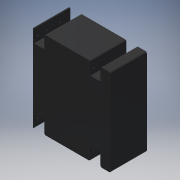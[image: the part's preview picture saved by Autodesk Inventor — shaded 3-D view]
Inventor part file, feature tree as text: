
AUTODESK INVENTOR PART (.ipt)
format: ipt  version: 2016 (Build 200138000, 138)  size: 579,072 bytes
history: native  units: mm
features: extrude x26, sketch x26, fillet x1
ambient origin geometry x8: Origin, YZ Plane, XZ Plane, XY Plane, X Axis, Y Axis, Z Axis, Center Point
bodies: Solid1 (feature_tree)
feature tree (53):
  extrude  "Extrusion1"  Depth=20.0mm
  extrude  "Extrusion2"  Depth=170.0mm
  extrude  "Extrusion3"  Depth=25.0mm
  extrude  "Extrusion4"  Depth=25.0mm
  extrude  "Extrusion5"  Depth=20.0mm
  extrude  "Extrusion6"  Depth=20.0mm
  extrude  "Extrusion7"  Depth=90.0mm
  extrude  "Extrusion8"  Depth=2.0mm TaperAngle=0.0deg
  extrude  "Extrusion9"  Depth=2.0mm
  extrude  "Extrusion10"  Depth=2.0mm
  extrude  "Extrusion11"  Depth=2.0mm
  extrude  "Extrusion12"  Depth=2.0mm
  extrude  "Extrusion13"  Depth=2.0mm
  extrude  "Extrusion14"  Depth=2.0mm
  extrude  "Extrusion15"  Depth=2.0mm
  extrude  "Extrusion16"  Depth=69.0mm TaperAngle=0.0deg
  extrude  "Extrusion17"  Depth=10.0mm TaperAngle=0.0deg
  extrude  "Extrusion18"  Depth=10.0mm
  extrude  "Extrusion32"  Depth=4.0mm TaperAngle=0.0deg
  extrude  "Extrusion33"  Depth=10.0mm
  extrude  "Extrusion34"  Depth=4.0mm TaperAngle=0.0deg
  extrude  "Extrusion35"  Depth=10.0mm
  extrude  "Extrusion53"  Depth=4.0mm TaperAngle=0.0deg
  fillet  "Fillet1"  Radius=7.0mm
  extrude  "Extrusion54"  Depth=10.0mm
  extrude  "Extrusion55"  Depth=4.0mm
  extrude  "Extrusion56"  Depth=2.0mm
  sketch  "Sketch1"  dims[d0=2.0mm d1=20.0mm]
  sketch  "Sketch2"  dims[d2=20.0mm d3=170.0mm]
  sketch  "Sketch4"  dims[d4=170.0mm d6=25.0mm]
  sketch  "Sketch5"  dims[d9=25.0mm d10=25.0mm]
  sketch  "Sketch6"  dims[d11=25.0mm d12=20.0mm]
  sketch  "Sketch7"  dims[d13=90.0mm d14=20.0mm]
  sketch  "Sketch8"  dims[d15=2.0mm d16=90.0mm]
  sketch  "Sketch9"  dims[d17=20.0mm d18=2.0mm d19=0.0mm]
  sketch  "Sketch10"  dims[d20=4.0mm d21=2.0mm]
  sketch  "Sketch11"  dims[d22=2.0mm d23=2.0mm]
  sketch  "Sketch12"  dims[d26=4.0mm d27=2.0mm]
  sketch  "Sketch13"  dims[d28=2.0mm d29=2.0mm]
  sketch  "Sketch14"  dims[d30=2.0mm d31=2.0mm]
  sketch  "Sketch15"  dims[d32=4.0mm d33=2.0mm]
  sketch  "Sketch16"  dims[d34=2.0mm d35=2.0mm]
  sketch  "Sketch17"  dims[d36=4.0mm d37=69.0mm d38=0.0mm]
  sketch  "Sketch18"  dims[d39=2.0mm d40=10.0mm d41=0.0mm]
  sketch  "Sketch19"  dims[d42=7.0mm d43=10.0mm]
  sketch  "Sketch33"  dims[d44=3.2mm d45=4.0mm d46=0.0mm]
  sketch  "Sketch34"  dims[d47=7.0mm d48=10.0mm]
  sketch  "Sketch35"  dims[d49=3.2mm d50=4.0mm d51=0.0mm]
  sketch  "Sketch36"  dims[d52=7.0mm d53=10.0mm]
  sketch  "Sketch55"  dims[d54=3.2mm d55=4.0mm d56=0.0mm d57=7.0mm]
  sketch  "Sketch56"  dims[d58=10.0mm d59=3.2mm]
  sketch  "Sketch57"  dims[d60=4.0mm d61=0.0mm d64=3.2mm]
  sketch  "Sketch58"  dims[d65=4.0mm d66=0.0mm d69=3.2mm d70=4.0mm d71=0.0mm d72=7.0mm d73=10.0mm d74=3.2mm d75=4.0mm d76=0.0mm d77=7.0mm d79=3.2mm d80=4.0mm d81=0.0mm d82=5.0mm d83=3.0mm d84=15.0mm d85=3.0mm d86=20.0mm d87=25.0mm d88=3.0mm d89=3.0mm d90=2.0mm d91=0.0mm d92=7.0mm d93=2.625mm d94=3.0mm d95=4.0mm d96=0.0mm d97=7.0mm d98=2.625mm d99=3.0mm d100=4.0mm d101=0.0mm d102=7.0mm d103=2.625mm d104=3.0mm d105=4.0mm d106=0.0mm d107=7.0mm d108=2.625mm d109=3.0mm d110=4.0mm d111=0.0mm d112=25.0mm d113=25.0mm d114=25.0mm d115=25.0mm d116=29.0mm d117=14.5mm d118=15.0mm d119=7.0mm d120=6.0mm d121=6.0mm d122=6.0mm d123=3.0mm d124=6.0mm d125=6.0mm d126=6.0mm d127=6.0mm d128=67.0mm d129=0.0mm d130=3.0mm d131=3.0mm d132=3.0mm d133=67.0mm d134=0.0mm d135=6.0mm d136=3.0mm d137=3.0mm d138=3.0mm d139=3.0mm d202=3.0mm d203=3.0mm d299=11.0mm d300=2.5mm d301=5.0mm d302=5.0mm d303=4.0mm d304=0.0mm d305=11.0mm d306=2.5mm d307=5.0mm d308=5.0mm d309=4.0mm d310=0.0mm d311=11.0mm d312=2.5mm d313=5.0mm d314=5.0mm d315=4.0mm d316=0.0mm d317=11.0mm d318=2.5mm d319=5.0mm d320=5.0mm d321=4.0mm d322=0.0mm d363=10.0mm d364=10.0mm d365=10.0mm d387=7.0mm d388=10.0mm d412=3.0mm d415=158.0mm d416=78.0mm d417=158.0mm d418=78.0mm d419=4.0mm d421=4.0mm d422=4.0mm d423=4.0mm d424=8.0mm d425=8.0mm d426=8.0mm d427=8.0mm d428=8.0mm d429=8.0mm d430=8.0mm d431=8.0mm d432=24.0mm d433=0.0mm d434=3.0mm d435=5.0mm d436=10.0mm d437=5.0mm d439=10.0mm d441=2.0mm d442=0.0mm d443=10.0mm d444=19.0mm d445=2.0mm d446=0.0mm d447=10.0mm d449=10.0mm d450=2.0mm d451=0.0mm]
